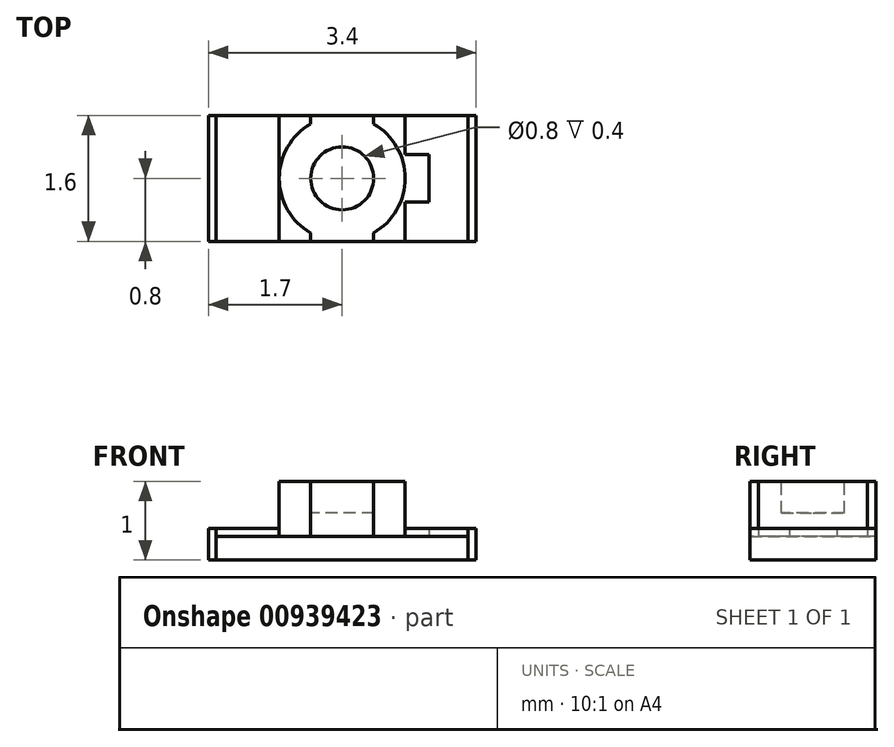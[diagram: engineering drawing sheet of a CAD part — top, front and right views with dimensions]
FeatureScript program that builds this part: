
annotation { "Feature Type Name" : "Feature", "Feature Type Description" : "" }
export const myFeature = defineFeature(function(context is Context, id is Id, definition is map)
    precondition{}
    {
        {
            var Q0;
            Q0=qCreatedBy(makeId("Top.planeOp"),FACE);
            var sketch = newSketch(context, id + "F0", { "sketchPlane" : qUnion([Q0])});
            skLineSegment(sketch, "E0.bottom", {"start": v(-1.6, 0.8) * mm, "end": v(1.6, 0.8) * mm});
            skLineSegment(sketch, "E0.top", {"start": v(-1.6, -0.8) * mm, "end": v(1.6, -0.8) * mm});
            skLineSegment(sketch, "E0.left", {"start": v(-1.6, 0.8) * mm, "end": v(-1.6, -0.8) * mm});
            skLineSegment(sketch, "E0.right", {"start": v(1.6, 0.8) * mm, "end": v(1.6, -0.8) * mm});
            skPoint(sketch, "E0.middle", {"position": v(0, 0) * mm});
            skSolve(sketch);
        }
        {
            var Q0;
            Q0 = qSketchRegion(id + "F0", true);
            extrude(context, id + "F1", {"entities" : qUnion([Q0]), "depth" : 0.3 * mm, "offsetDistance" : 25 * mm});
        }
        {
            var Q0;
            Q0=makeQuery(id+"F1.opExtrude","CAP_FACE",FACE,{"disambiguationData":[OSD([sQuery(id+"F0.wireOp",EDGE,"E0.bottom"),sQuery(id+"F0.wireOp",EDGE,"E0.top"),sQuery(id+"F0.wireOp",EDGE,"E0.left"),sQuery(id+"F0.wireOp",EDGE,"E0.right")])],"isStart":false});
            var sketch = newSketch(context, id + "F2", { "sketchPlane" : qUnion([Q0])});
            skLineSegment(sketch, "E1.bottom", {"start": v(-1.6, -0.8) * mm, "end": v(-0.8, -0.8) * mm});
            skLineSegment(sketch, "E1.top", {"start": v(-1.6, 0.8) * mm, "end": v(-0.8, 0.8) * mm});
            skLineSegment(sketch, "E1.left", {"start": v(-1.6, -0.8) * mm, "end": v(-1.6, 0.8) * mm});
            skLineSegment(sketch, "E1.right", {"start": v(-0.8, -0.8) * mm, "end": v(-0.8, 0.8) * mm});
            skLineSegment(sketch, "E2", {"start": v(0.8, -0.8) * mm, "end": v(1.6, -0.8) * mm});
            skLineSegment(sketch, "E3", {"start": v(1.6, -0.8) * mm, "end": v(1.6, 0.8) * mm});
            skLineSegment(sketch, "E4", {"start": v(1.6, 0.8) * mm, "end": v(0.8, 0.8) * mm});
            skLineSegment(sketch, "E5", {"start": v(0.8, 0.8) * mm, "end": v(0.8, 0.3) * mm});
            skLineSegment(sketch, "E6", {"start": v(0.8, 0.3) * mm, "end": v(1.1, 0.3) * mm});
            skLineSegment(sketch, "E7", {"start": v(1.1, 0.3) * mm, "end": v(1.1, -0.3) * mm});
            skLineSegment(sketch, "E8", {"start": v(1.1, -0.3) * mm, "end": v(0.8, -0.3) * mm});
            skLineSegment(sketch, "E9", {"start": v(0.8, -0.3) * mm, "end": v(0.8, -0.8) * mm});
            skSolve(sketch);
        }
        {
            var Q0;
            Q0 = qSketchRegion(id + "F2", true);
            extrude(context, id + "F3", {"entities" : qUnion([Q0]), "depth" : 0.1 * mm, "offsetDistance" : 25 * mm});
        }
        {
            var Q0;
            Q0=makeQuery(id+"F1.opExtrude","SWEPT_FACE",FACE,{"disambiguationData":[OSD([sQuery(id+"F0.wireOp",EDGE,"E0.left")])]});
            var sketch = newSketch(context, id + "F4", { "sketchPlane" : qUnion([Q0])});
            skLineSegment(sketch, "E10.bottom", {"start": v(-0.8, 0) * mm, "end": v(0.8, 0) * mm});
            skLineSegment(sketch, "E10.top", {"start": v(-0.8, 0.4) * mm, "end": v(0.8, 0.4) * mm});
            skLineSegment(sketch, "E10.left", {"start": v(-0.8, 0) * mm, "end": v(-0.8, 0.4) * mm});
            skLineSegment(sketch, "E10.right", {"start": v(0.8, 0) * mm, "end": v(0.8, 0.4) * mm});
            skSolve(sketch);
        }
        {
            var Q0;
            Q0 = qSketchRegion(id + "F4", true);
            extrude(context, id + "F5", {"entities" : qUnion([Q0]), "depth" : 0.1 * mm, "offsetDistance" : 25 * mm});
        }
        {
            var Q0;
            Q0=makeQuery(id+"F1.opExtrude","SWEPT_FACE",FACE,{"disambiguationData":[OSD([sQuery(id+"F0.wireOp",EDGE,"E0.right")])]});
            var sketch = newSketch(context, id + "F6", { "sketchPlane" : qUnion([Q0])});
            skLineSegment(sketch, "E11.bottom", {"start": v(-0.8, 0) * mm, "end": v(0.8, 0) * mm});
            skLineSegment(sketch, "E11.top", {"start": v(-0.8, 0.4) * mm, "end": v(0.8, 0.4) * mm});
            skLineSegment(sketch, "E11.left", {"start": v(-0.8, 0) * mm, "end": v(-0.8, 0.4) * mm});
            skLineSegment(sketch, "E11.right", {"start": v(0.8, 0) * mm, "end": v(0.8, 0.4) * mm});
            skSolve(sketch);
        }
        {
            var Q0;
            Q0 = qSketchRegion(id + "F6", true);
            extrude(context, id + "F7", {"entities" : qUnion([Q0]), "depth" : 0.1 * mm, "offsetDistance" : 25 * mm});
        }
        {
            var Q0;
            Q0=makeQuery(id+"F1.opExtrude","CAP_FACE",FACE,{"disambiguationData":[OSD([sQuery(id+"F0.wireOp",EDGE,"E0.bottom"),sQuery(id+"F0.wireOp",EDGE,"E0.top"),sQuery(id+"F0.wireOp",EDGE,"E0.left"),sQuery(id+"F0.wireOp",EDGE,"E0.right")])],"isStart":false});
            var sketch = newSketch(context, id + "F8", { "sketchPlane" : qUnion([Q0])});
            skArc(sketch, "E12", {"start": v(-0.4, 0.7) * mm, "mid": v(-0.8, 0) * mm, "end": v(-0.4, -0.7) * mm});
            skArc(sketch, "E13", {"start": v(0.4, 0.7) * mm, "mid": v(0.8, 0) * mm, "end": v(0.4, -0.7) * mm});
            skLineSegment(sketch, "E14", {"start": v(-0.4, 0.7) * mm, "end": v(-0.4, 0.8) * mm});
            skLineSegment(sketch, "E15", {"start": v(-0.4, 0.8) * mm, "end": v(0.4, 0.8) * mm});
            skLineSegment(sketch, "E16", {"start": v(0.4, 0.8) * mm, "end": v(0.4, 0.7) * mm});
            skLineSegment(sketch, "E17", {"start": v(0.4, -0.7) * mm, "end": v(0.4, -0.8) * mm});
            skLineSegment(sketch, "E18", {"start": v(0.4, -0.8) * mm, "end": v(-0.4, -0.8) * mm});
            skLineSegment(sketch, "E19", {"start": v(-0.4, -0.8) * mm, "end": v(-0.4, -0.7) * mm});
            skSolve(sketch);
        }
        {
            var Q0;
            Q0 = qSketchRegion(id + "F8", true);
            extrude(context, id + "F9", {"entities" : qUnion([Q0]), "depth" : 0.7 * mm, "offsetDistance" : 25 * mm});
        }
        {
            var Q0;
            Q0=makeQuery(id+"F9.opExtrude","CAP_FACE",FACE,{"disambiguationData":[OSD([sQuery(id+"F8.wireOp",EDGE,"E12"),sQuery(id+"F8.wireOp",EDGE,"E13"),sQuery(id+"F8.wireOp",EDGE,"E14"),sQuery(id+"F8.wireOp",EDGE,"E15"),sQuery(id+"F8.wireOp",EDGE,"E16"),sQuery(id+"F8.wireOp",EDGE,"E17"),sQuery(id+"F8.wireOp",EDGE,"E18"),sQuery(id+"F8.wireOp",EDGE,"E19")])],"isStart":false});
            var sketch = newSketch(context, id + "F10", { "sketchPlane" : qUnion([Q0])});
            skCircle(sketch, "E20", {"center": v(0, 0) * mm, "radius": 0.4 * mm});
            skSolve(sketch);
        }
        {
            var Q0;
            Q0 = qSketchRegion(id + "F10", true);
            extrude(context, id + "F11", {"entities" : qUnion([Q0]), "operationType" : NewBodyOperationType.REMOVE, "oppositeDirection" : true, "depth" : 0.4 * mm, "offsetDistance" : 25 * mm});
        }
    });
